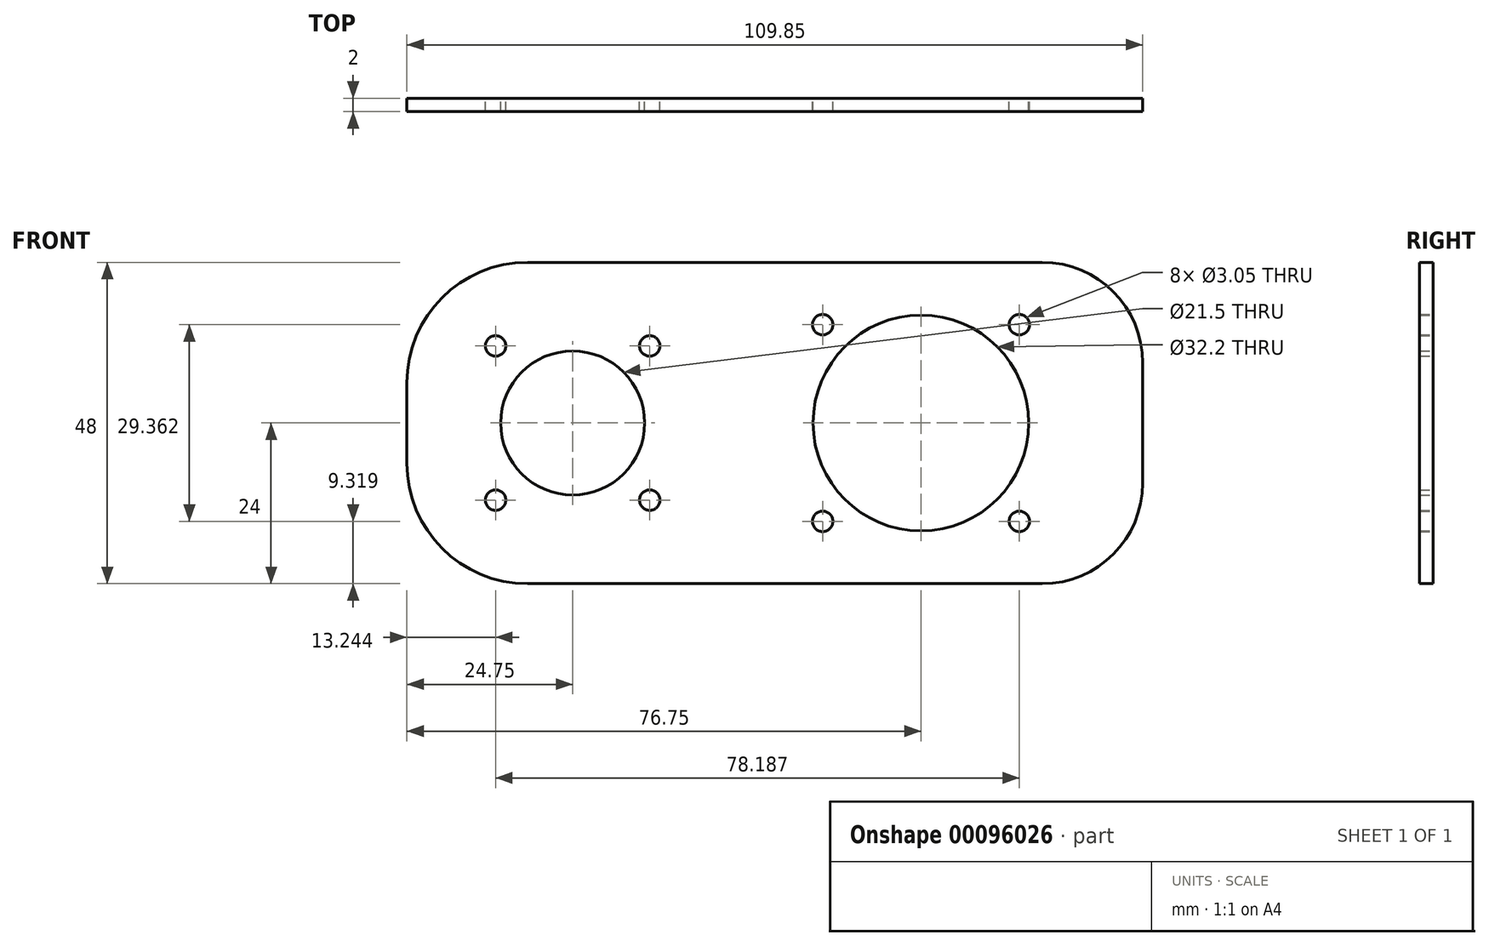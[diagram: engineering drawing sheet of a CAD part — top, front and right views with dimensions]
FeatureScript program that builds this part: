
annotation { "Feature Type Name" : "Feature", "Feature Type Description" : "" }
export const myFeature = defineFeature(function(context is Context, id is Id, definition is map)
    precondition{}
    {
        {
            var Q0;
            Q0=qCreatedBy(makeId("Front.planeOp"),FACE);
            var sketch = newSketch(context, id + "F0", { "sketchPlane" : qUnion([Q0])});
            skCircle(sketch, "E0", {"center": v(11.5, 11.5) * mm, "radius": 1.52 * mm});
            skCircle(sketch, "E1.MirrorC", {"center": v(-11.5, 11.5) * mm, "radius": 1.52 * mm});
            skCircle(sketch, "E2.MirrorC", {"center": v(11.5, -11.5) * mm, "radius": 1.52 * mm});
            skCircle(sketch, "E3.MirrorC", {"center": v(-11.5, -11.5) * mm, "radius": 1.52 * mm});
            skCircle(sketch, "E4", {"center": v(0, 0) * mm, "radius": 10.75 * mm});
            skCircle(sketch, "E5", {"center": v(66.68, 14.68) * mm, "radius": 1.52 * mm});
            skCircle(sketch, "E6", {"center": v(52, 0) * mm, "radius": 16.1 * mm});
            skLineSegment(sketch, "E7", {"start": v(52, 30.14) * mm, "end": v(52, 0) * mm, "construction": true});
            skLineSegment(sketch, "E8", {"start": v(52, 0) * mm, "end": v(75.73, 0) * mm, "construction": true});
            skCircle(sketch, "E9.MirrorC", {"center": v(37.32, 14.68) * mm, "radius": 1.52 * mm});
            skCircle(sketch, "E10.MirrorC", {"center": v(66.68, -14.68) * mm, "radius": 1.52 * mm});
            skCircle(sketch, "E11.MirrorC", {"center": v(37.32, -14.68) * mm, "radius": 1.52 * mm});
            skLineSegment(sketch, "E12", {"start": v(-24.75, 0) * mm, "end": v(-24.75, 6) * mm});
            skLineSegment(sketch, "E13", {"start": v(-6.75, 24) * mm, "end": v(70.1, 24) * mm});
            skLineSegment(sketch, "E14", {"start": v(85.1, 9) * mm, "end": v(85.1, 0) * mm});
            skLineSegment(sketch, "E15", {"start": v(0, 0) * mm, "end": v(52, 0) * mm, "construction": true});
            skLineSegment(sketch, "E16.MirrorCS", {"start": v(85.1, -9) * mm, "end": v(85.1, 0) * mm});
            skLineSegment(sketch, "E17.MirrorCS", {"start": v(-24.75, 0) * mm, "end": v(-24.75, -6) * mm});
            skLineSegment(sketch, "E18.MirrorCS", {"start": v(-6.75, -24) * mm, "end": v(70.1, -24) * mm});
            skPoint(sketch, "E19.visualSharp", {"position": v(-24.75, 24) * mm});
            skArc(sketch, "E19.filletArc", {"start": v(-6.75, 24) * mm, "mid": v(-19.48, 18.73) * mm, "end": v(-24.75, 6) * mm});
            skPoint(sketch, "E20.visualSharp", {"position": v(-24.75, -24) * mm});
            skArc(sketch, "E20.filletArc", {"start": v(-24.75, -6) * mm, "mid": v(-19.48, -18.73) * mm, "end": v(-6.75, -24) * mm});
            skPoint(sketch, "E21.visualSharp", {"position": v(85.1, -24) * mm});
            skArc(sketch, "E21.filletArc", {"start": v(70.1, -24) * mm, "mid": v(80.7, -19.6) * mm, "end": v(85.1, -9) * mm});
            skPoint(sketch, "E22.visualSharp", {"position": v(85.1, 24) * mm});
            skArc(sketch, "E22.filletArc", {"start": v(85.1, 9) * mm, "mid": v(80.7, 19.6) * mm, "end": v(70.1, 24) * mm});
            skSolve(sketch);
        }
        {
            var Q0;
            Q0 = qSketchRegion(id + "F0", true);
            extrude(context, id + "F1", {"entities" : qUnion([Q0]), "depth" : 2 * mm});
        }
    });
